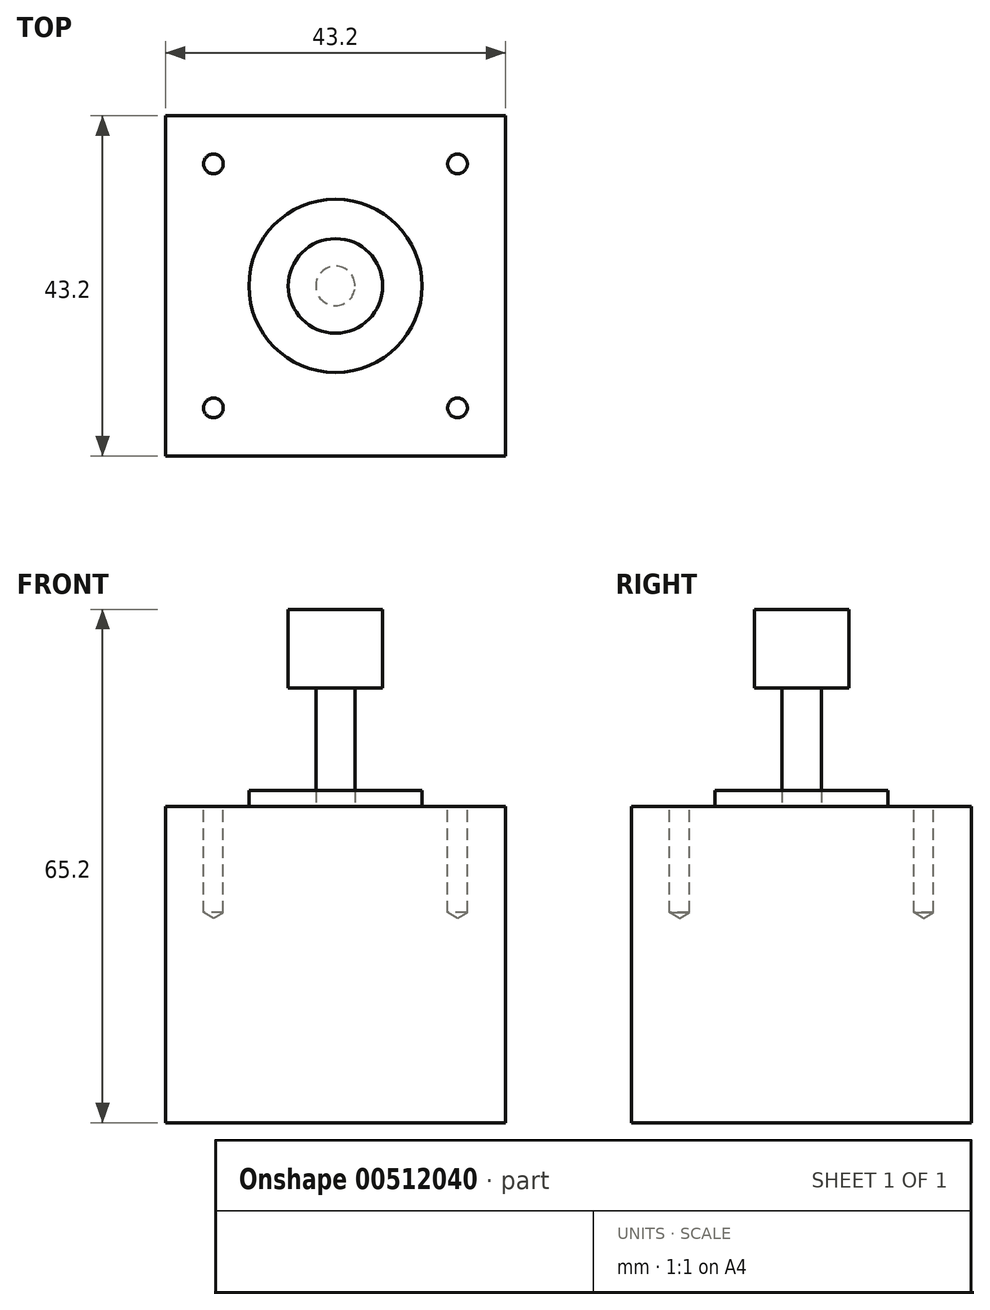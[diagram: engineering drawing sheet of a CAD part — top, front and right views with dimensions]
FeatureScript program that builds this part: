
annotation { "Feature Type Name" : "Feature", "Feature Type Description" : "" }
export const myFeature = defineFeature(function(context is Context, id is Id, definition is map)
    precondition{}
    {
        {
            var Q0;
            Q0=qCreatedBy(makeId("Top.planeOp"),FACE);
            var sketch = newSketch(context, id + "F0", { "sketchPlane" : qUnion([Q0])});
            skLineSegment(sketch, "E0.bottom", {"start": v(-21.6, 21.6) * mm, "end": v(21.6, 21.6) * mm});
            skLineSegment(sketch, "E0.top", {"start": v(-21.6, -21.6) * mm, "end": v(21.6, -21.6) * mm});
            skLineSegment(sketch, "E0.left", {"start": v(-21.6, 21.6) * mm, "end": v(-21.6, -21.6) * mm});
            skLineSegment(sketch, "E0.right", {"start": v(21.6, 21.6) * mm, "end": v(21.6, -21.6) * mm});
            skPoint(sketch, "E0.middle", {"position": v(0, 0) * mm});
            skLineSegment(sketch, "E1", {"start": v(0, -21.6) * mm, "end": v(0, 21.6) * mm, "construction": true});
            skLineSegment(sketch, "E2", {"start": v(21.6, 0) * mm, "end": v(-21.6, 0) * mm, "construction": true});
            skSolve(sketch);
        }
        {
            var Q0;
            Q0=qSketchRegion(id+"F0",true);
            extrude(context, id + "F1", {"entities" : qUnion([Q0]), "depth" : 40.2 * mm});
        }
        {
            var Q0;
            Q0=makeQuery(id+"F1.opExtrude","CAP_FACE",FACE,{"disambiguationData":[OSD([sQuery(id+"F0.wireOp",EDGE,"E0.bottom"),sQuery(id+"F0.wireOp",EDGE,"E0.top"),sQuery(id+"F0.wireOp",EDGE,"E0.left"),sQuery(id+"F0.wireOp",EDGE,"E0.right")])],"isStart":false});
            var sketch = newSketch(context, id + "F2", { "sketchPlane" : qUnion([Q0])});
            skCircle(sketch, "E3", {"center": v(0, 0) * mm, "radius": 2.5 * mm});
            skLineSegment(sketch, "E4", {"start": v(-15.5, -21.6) * mm, "end": v(-15.5, 21.6) * mm, "construction": true});
            skLineSegment(sketch, "E5", {"start": v(15.5, -21.6) * mm, "end": v(15.5, 21.6) * mm, "construction": true});
            skLineSegment(sketch, "E6", {"start": v(-21.6, -15.5) * mm, "end": v(21.6, -15.5) * mm, "construction": true});
            skLineSegment(sketch, "E7", {"start": v(-21.6, 15.5) * mm, "end": v(21.6, 15.5) * mm, "construction": true});
            skLineSegment(sketch, "E8", {"start": v(0, 21.6) * mm, "end": v(0, -21.6) * mm, "construction": true});
            skLineSegment(sketch, "E9", {"start": v(-21.6, 0) * mm, "end": v(21.6, 0) * mm, "construction": true});
            skLineSegment(sketch, "E10", {"start": v(0, 17.18) * mm, "end": v(-15.5, 17.18) * mm});
            skLineSegment(sketch, "E11", {"start": v(0, 17.18) * mm, "end": v(15.5, 17.18) * mm});
            skLineSegment(sketch, "E12", {"start": v(-5.66, -15.5) * mm, "end": v(-5.66, 0) * mm});
            skLineSegment(sketch, "E13", {"start": v(-5.66, 0) * mm, "end": v(-5.66, 15.5) * mm});
            skCircle(sketch, "E14", {"center": v(-15.5, -15.5) * mm, "radius": 1.5 * mm});
            skCircle(sketch, "E15", {"center": v(-15.5, 15.5) * mm, "radius": 1.5 * mm});
            skCircle(sketch, "E16", {"center": v(15.5, -15.5) * mm, "radius": 1.5 * mm});
            skCircle(sketch, "E17", {"center": v(15.5, 15.5) * mm, "radius": 1.5 * mm});
            skSolve(sketch);
        }
        {
            var Q0;
            Q0=makeQuery(id+"F2.imprint","IMPRINT",FACE,{"disambiguationData":[TD([[makeQuery(id+"F2.imprint","IMPRINT",EDGE,{"derivedFrom":sQuery(id+"F2.wireOp",EDGE,"E3")}),1.0]])]});
            extrude(context, id + "F3", {"entities" : qUnion([Q0]), "depth" : 25 * mm});
        }
        {
            var Q0;
            Q0=sQuery(id+"F2.wireOp",VERTEX,"E14.center");
            var Q1;
            Q1=sQuery(id+"F2.wireOp",VERTEX,"E15.center");
            var Q2;
            Q2=sQuery(id+"F2.wireOp",VERTEX,"E17.center");
            var Q3;
            Q3=sQuery(id+"F2.wireOp",VERTEX,"E16.center");
            var Q4;
            Q4=makeQuery(id+"F1.opExtrude","SWEPT_BODY",BODY,{"disambiguationData":[OSD([sQuery(id+"F0.wireOp",EDGE,"E0.bottom"),sQuery(id+"F0.wireOp",EDGE,"E0.top"),sQuery(id+"F0.wireOp",EDGE,"E0.left"),sQuery(id+"F0.wireOp",EDGE,"E0.right")])]});
            hole(context, id + "F4", {"style" : HoleStyle.SIMPLE, "endStyle" : HoleEndStyle.BLIND, "standardTappedOrClearance" : lookupTablePath({ "standard" : "ISO", "engagement" : "75%", "pitch" : "0.5 mm", "size" : "M3", "type" : "Tapped" }), "standardBlindInLast" : lookupTablePath({ "standard" : "ISO", "engagement" : "75%", "pitch" : "0.5 mm", "size" : "M3", "type" : "Tapped" }), "holeDiameter" : 2.5 * mm, "showTappedDepth" : true, "holeDepth" : 13.5 * mm, "isTappedThrough" : true, "tappedDepth" : 12 * mm, "tapClearance" : 3, "locations" : qUnion([Q0, Q1, Q2, Q3]), "scope" : qUnion([Q4]), "majorDiameter" : 3 * mm});
        }
        {
            var Q0;
            Q0=makeQuery(id+"F1.opExtrude","CAP_FACE",FACE,{"disambiguationData":[OSD([sQuery(id+"F0.wireOp",EDGE,"E0.bottom"),sQuery(id+"F0.wireOp",EDGE,"E0.top"),sQuery(id+"F0.wireOp",EDGE,"E0.left"),sQuery(id+"F0.wireOp",EDGE,"E0.right")])],"isStart":false});
            var sketch = newSketch(context, id + "F5", { "sketchPlane" : qUnion([Q0])});
            skCircle(sketch, "E18", {"center": v(0, 0) * mm, "radius": 11 * mm});
            skSolve(sketch);
        }
        {
            var Q0;
            Q0=makeQuery(id+"F5.imprint","IMPRINT",FACE,{"disambiguationData":[TD([[makeQuery(id+"F5.imprint","IMPRINT",EDGE,{"derivedFrom":sQuery(id+"F5.wireOp",EDGE,"E18")}),1.0]])]});
            extrude(context, id + "F6", {"entities" : qUnion([Q0]), "depth" : 2 * mm});
        }
        {
            var Q0;
            Q0=makeQuery(id+"F3.opExtrude","CAP_FACE",FACE,{"disambiguationData":[OSD([sQuery(id+"F2.wireOp",EDGE,"E3")])],"isStart":false});
            var sketch = newSketch(context, id + "F7", { "sketchPlane" : qUnion([Q0])});
            skCircle(sketch, "E19", {"center": v(0, 0) * mm, "radius": 6 * mm});
            skSolve(sketch);
        }
        {
            var Q0;
            Q0=qSketchRegion(id+"F7",true);
            extrude(context, id + "F8", {"entities" : qUnion([Q0]), "operationType" : NewBodyOperationType.ADD, "oppositeDirection" : true, "depth" : 10 * mm});
        }
    });
